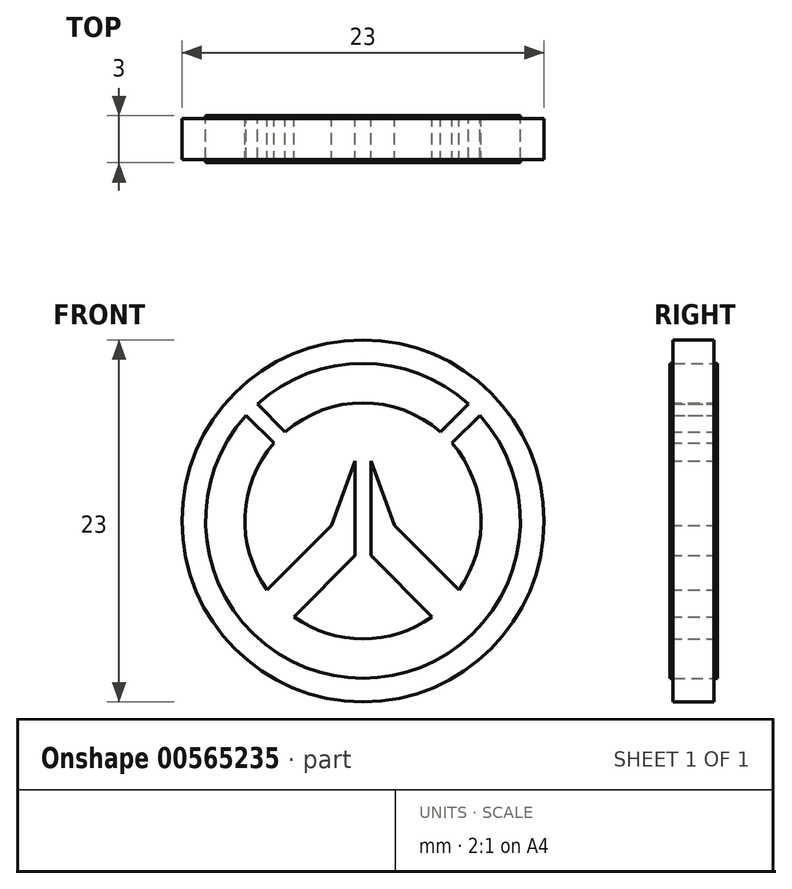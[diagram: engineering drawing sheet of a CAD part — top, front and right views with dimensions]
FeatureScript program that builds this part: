
annotation { "Feature Type Name" : "Feature", "Feature Type Description" : "" }
export const myFeature = defineFeature(function(context is Context, id is Id, definition is map)
    precondition{}
    {
        {
            var Q0;
            Q0=qCreatedBy(makeId("Front.planeOp"),FACE);
            var sketch = newSketch(context, id + "F0", { "sketchPlane" : qUnion([Q0])});
            skCircle(sketch, "E0", {"center": v(0, 0) * mm, "radius": 10 * mm});
            skCircle(sketch, "E1.0", {"center": v(0, 0) * mm, "radius": 7.5 * mm});
            skLineSegment(sketch, "E2", {"start": v(0, 0) * mm, "end": v(-7.07, 7.07) * mm, "construction": true});
            skLineSegment(sketch, "E3", {"start": v(0, 0) * mm, "end": v(7.07, 7.07) * mm, "construction": true});
            skLineSegment(sketch, "E4", {"start": v(0, 0) * mm, "end": v(0, 10) * mm, "construction": true});
            skLineSegment(sketch, "E5.0", {"start": v(0, -0.7) * mm, "end": v(-7.42, 6.7) * mm});
            skLineSegment(sketch, "E5.1", {"start": v(0, -0.7) * mm, "end": v(7.42, 6.7) * mm});
            skLineSegment(sketch, "E6.0", {"start": v(0, 0.7) * mm, "end": v(-6.7, 7.42) * mm});
            skLineSegment(sketch, "E6.1", {"start": v(0, 0.7) * mm, "end": v(6.7, 7.42) * mm});
            skSolve(sketch);
        }
        {
            var Q0;
            {var subQ0=sQuery(id+"F0.wireOp",EDGE,"E5.0");var subQ1=sQuery(id+"F0.wireOp",EDGE,"E0");var subQ2=makeQuery(id+"F0.imprint","INTERSECT",VERTEX,{"derivedFrom":[subQ1,subQ0]});Q0=makeQuery(id+"F0.imprint","IMPRINT",FACE,{"disambiguationData":[TD([[makeQuery(id+"F0.imprint","IMPRINT",EDGE,{"disambiguationData":[TD([[subQ2,-1.0]])],"derivedFrom":subQ1}),1.0]])]});}
            extrude(context, id + "F1", {"entities" : qUnion([Q0]), "depth" : 3 * mm});
        }
        {
            var Q0;
            {var subQ0=sQuery(id+"F0.wireOp",EDGE,"E6.0");var subQ1=sQuery(id+"F0.wireOp",EDGE,"E0");var subQ2=makeQuery(id+"F0.imprint","INTERSECT",VERTEX,{"derivedFrom":[subQ1,subQ0]});Q0=makeQuery(id+"F0.imprint","IMPRINT",FACE,{"disambiguationData":[TD([[makeQuery(id+"F0.imprint","IMPRINT",EDGE,{"disambiguationData":[TD([[subQ2,1.0]])],"derivedFrom":subQ1}),1.0]])]});}
            var Q1;
            Q1=makeQuery(id+"F1.opExtrude","CAP_FACE",FACE,{"disambiguationData":[OSD([sQuery(id+"F0.wireOp",EDGE,"E0"),sQuery(id+"F0.wireOp",EDGE,"E1.0"),sQuery(id+"F0.wireOp",EDGE,"E5.0"),sQuery(id+"F0.wireOp",EDGE,"E5.1")])],"isStart":false});
            extrude(context, id + "F2", {"entities" : qUnion([Q0]), "endBound" : BoundingType.UP_TO_SURFACE, "endBoundEntityFace" : qUnion([Q1]), "depth" : 25 * mm});
        }
        {
            var Q0;
            Q0=qCreatedBy(makeId("Front.planeOp"),FACE);
            var sketch = newSketch(context, id + "F3", { "sketchPlane" : qUnion([Q0])});
            skArc(sketch, "E7.0", {"start": v(-5.65, 4.94) * mm, "mid": v(0, -7.5) * mm, "end": v(5.65, 4.94) * mm});
            skLineSegment(sketch, "E8", {"start": v(0, 0) * mm, "end": v(-5.3, -5.3) * mm});
            skLineSegment(sketch, "E9", {"start": v(0, 0) * mm, "end": v(5.3, -5.3) * mm});
            skLineSegment(sketch, "E10", {"start": v(0, 0) * mm, "end": v(0, -7.5) * mm, "construction": true});
            skLineSegment(sketch, "E11.0", {"start": v(0, 1.7) * mm, "end": v(-6.13, -4.43) * mm});
            skLineSegment(sketch, "E11.1", {"start": v(0, 1.7) * mm, "end": v(6.15, -4.45) * mm});
            skLineSegment(sketch, "E12.0", {"start": v(0, -1.7) * mm, "end": v(-4.45, -6.15) * mm});
            skLineSegment(sketch, "E12.1", {"start": v(0, -1.7) * mm, "end": v(4.45, -6.15) * mm});
            skLineSegment(sketch, "E13", {"start": v(0, -1.7) * mm, "end": v(0, 3.8) * mm, "construction": true});
            skLineSegment(sketch, "E14.0", {"start": v(0.5, -2.2) * mm, "end": v(0.5, 3.8) * mm});
            skLineSegment(sketch, "E15.0", {"start": v(-0.5, -2.2) * mm, "end": v(-0.5, 3.8) * mm});
            skLineSegment(sketch, "E16", {"start": v(-0.5, 3.8) * mm, "end": v(-2, -0.3) * mm});
            skLineSegment(sketch, "E17", {"start": v(0.5, 3.8) * mm, "end": v(2, -0.3) * mm});
            skSolve(sketch);
        }
        {
            var Q0;
            {var subQ4=sQuery(id+"F3.wireOp",EDGE,"E8");var subQ5=sQuery(id+"F3.wireOp",EDGE,"E7.0");var subQ6=makeQuery(id+"F3.imprint","INTERSECT",VERTEX,{"derivedFrom":[subQ5,subQ4]});Q0=makeQuery(id+"F3.imprint","IMPRINT",FACE,{"disambiguationData":[TD([[makeQuery(id+"F3.imprint","IMPRINT",EDGE,{"disambiguationData":[TD([[subQ6,1.0]])],"derivedFrom":subQ5}),1.0]])]});}
            var Q1;
            {var subQ0=sQuery(id+"F3.wireOp",EDGE,"E8");var subQ1=sQuery(id+"F3.wireOp",EDGE,"E7.0");var subQ2=makeQuery(id+"F3.imprint","INTERSECT",VERTEX,{"derivedFrom":[subQ1,subQ0]});Q1=makeQuery(id+"F3.imprint","IMPRINT",FACE,{"disambiguationData":[TD([[makeQuery(id+"F3.imprint","IMPRINT",EDGE,{"disambiguationData":[TD([[subQ2,-1.0]])],"derivedFrom":subQ1}),1.0]])]});}
            var Q2;
            {var subQ0=sQuery(id+"F3.wireOp",EDGE,"E16");Q2=makeQuery(id+"F3.imprint","IMPRINT",FACE,{"disambiguationData":[TD([[makeQuery(id+"F3.imprint","IMPRINT",EDGE,{"derivedFrom":subQ0}),1.0]])]});}
            var Q3;
            {var subQ2=sQuery(id+"F3.wireOp",EDGE,"E7.0");var subQ4=sQuery(id+"F3.wireOp",EDGE,"E9");var subQ5=makeQuery(id+"F3.imprint","INTERSECT",VERTEX,{"derivedFrom":[subQ2,subQ4]});Q3=makeQuery(id+"F3.imprint","IMPRINT",FACE,{"disambiguationData":[TD([[makeQuery(id+"F3.imprint","IMPRINT",EDGE,{"disambiguationData":[TD([[subQ5,-1.0]])],"derivedFrom":subQ2}),1.0]])]});}
            var Q4;
            {var subQ0=sQuery(id+"F3.wireOp",EDGE,"E9");var subQ1=sQuery(id+"F3.wireOp",EDGE,"E7.0");var subQ2=makeQuery(id+"F3.imprint","INTERSECT",VERTEX,{"derivedFrom":[subQ1,subQ0]});Q4=makeQuery(id+"F3.imprint","IMPRINT",FACE,{"disambiguationData":[TD([[makeQuery(id+"F3.imprint","IMPRINT",EDGE,{"disambiguationData":[TD([[subQ2,1.0]])],"derivedFrom":subQ1}),1.0]])]});}
            var Q5;
            {var subQ0=sQuery(id+"F3.wireOp",EDGE,"E17");Q5=makeQuery(id+"F3.imprint","IMPRINT",FACE,{"disambiguationData":[TD([[makeQuery(id+"F3.imprint","IMPRINT",EDGE,{"derivedFrom":subQ0}),-1.0]])]});}
            var Q6;
            Q6=makeQuery(id+"F1.opExtrude","CAP_FACE",FACE,{"disambiguationData":[OSD([sQuery(id+"F0.wireOp",EDGE,"E0"),sQuery(id+"F0.wireOp",EDGE,"E1.0"),sQuery(id+"F0.wireOp",EDGE,"E5.0"),sQuery(id+"F0.wireOp",EDGE,"E5.1")])],"isStart":false});
            extrude(context, id + "F4", {"entities" : qUnion([Q0, Q1, Q2, Q3, Q4, Q5]), "operationType" : NewBodyOperationType.ADD, "endBound" : BoundingType.UP_TO_SURFACE, "endBoundEntityFace" : qUnion([Q6]), "depth" : 25 * mm});
        }
        {
            var Q0;
            {var subQ0=sQuery(id+"F3.wireOp",EDGE,"E7.0");Q0=makeQuery(id+"F4.boolean.opBoolean","MERGE",FACE,{"derivedFrom":[makeQuery(id+"F1.opExtrude","CAP_FACE",FACE,{"disambiguationData":[OSD([sQuery(id+"F0.wireOp",EDGE,"E0"),sQuery(id+"F0.wireOp",EDGE,"E1.0"),sQuery(id+"F0.wireOp",EDGE,"E5.0"),sQuery(id+"F0.wireOp",EDGE,"E5.1")])],"isStart":true}),makeQuery(id+"F4.opExtrude","CAP_FACE",FACE,{"disambiguationData":[OSD([subQ0,sQuery(id+"F3.wireOp",EDGE,"E11.0"),sQuery(id+"F3.wireOp",EDGE,"E12.0"),sQuery(id+"F3.wireOp",EDGE,"E15.0"),sQuery(id+"F3.wireOp",EDGE,"E16")])],"isStart":true}),makeQuery(id+"F4.opExtrude","CAP_FACE",FACE,{"disambiguationData":[OSD([subQ0,sQuery(id+"F3.wireOp",EDGE,"E11.1"),sQuery(id+"F3.wireOp",EDGE,"E12.1"),sQuery(id+"F3.wireOp",EDGE,"E14.0"),sQuery(id+"F3.wireOp",EDGE,"E17")])],"isStart":true})]});}
            cPlane(context, id + "F5", {"entities" : qUnion([Q0]), "cplaneType" : CPlaneType.OFFSET, "offset" : 0.2 * mm, "oppositeDirection" : true, "width" : 150 * mm, "height" : 150 * mm});
        }
        {
            var Q0;
            Q0=qCreatedBy(id+"F5.planeOp",FACE);
            var sketch = newSketch(context, id + "F6", { "sketchPlane" : qUnion([Q0])});
            skCircle(sketch, "E18", {"center": v(0, 0) * mm, "radius": 11.5 * mm});
            skSolve(sketch);
        }
        {
            var Q0;
            Q0=makeQuery(id+"F6.imprint","IMPRINT",FACE,{"disambiguationData":[TD([[makeQuery(id+"F6.imprint","IMPRINT",EDGE,{"derivedFrom":sQuery(id+"F6.wireOp",EDGE,"E18")}),1.0]])]});
            extrude(context, id + "F7", {"entities" : qUnion([Q0]), "oppositeDirection" : true, "depth" : 2.6 * mm, "offsetDistance" : 25 * mm});
        }
    });
